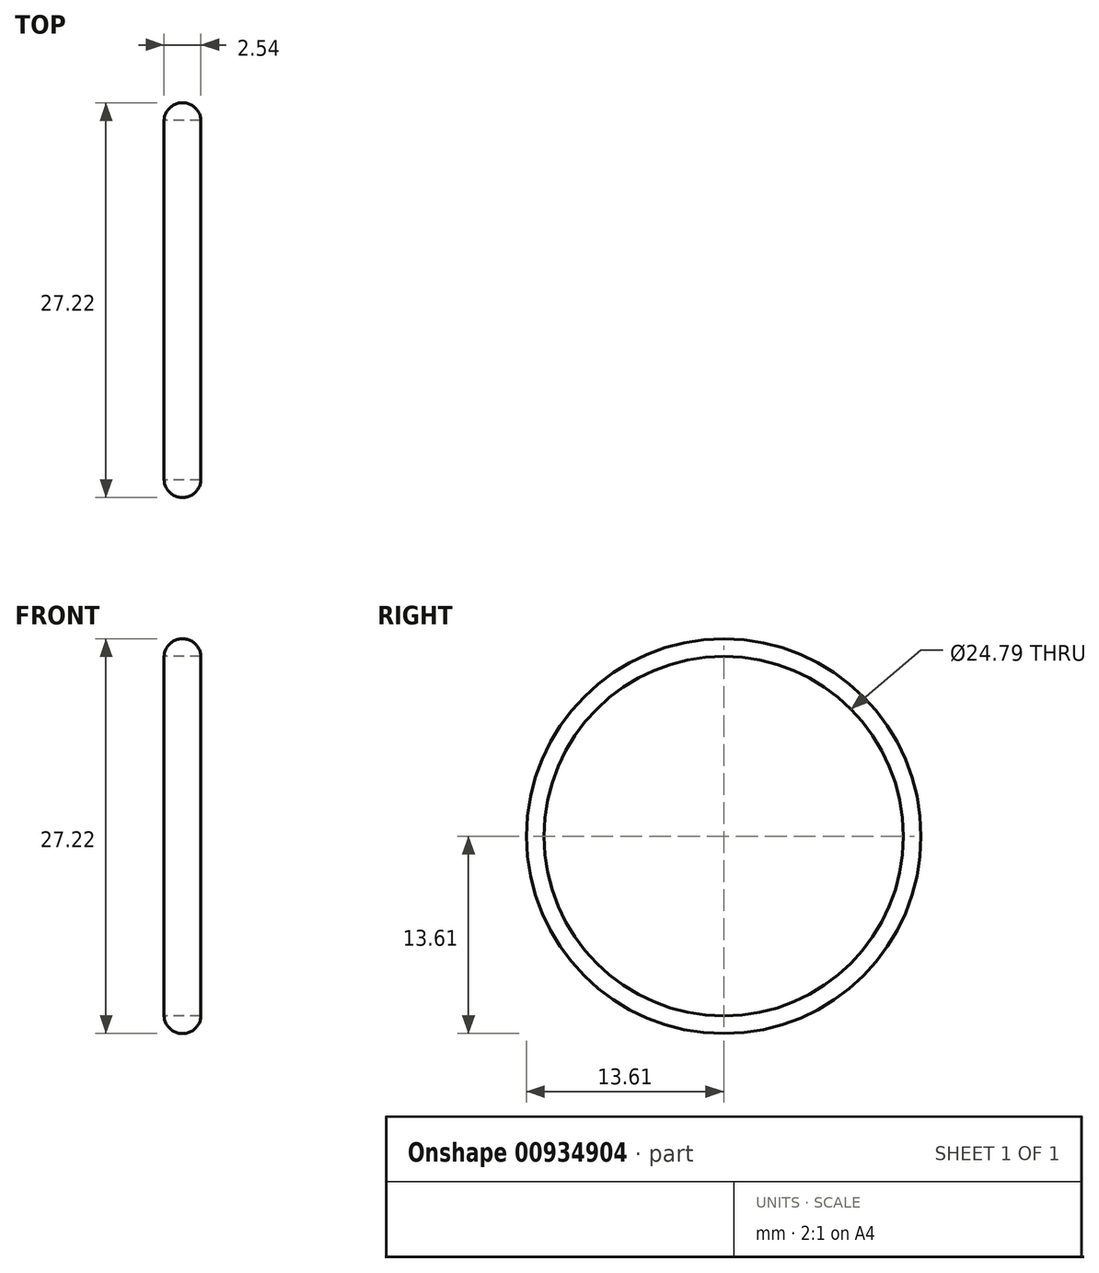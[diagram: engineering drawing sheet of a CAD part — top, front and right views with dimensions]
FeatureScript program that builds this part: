
annotation { "Feature Type Name" : "Feature", "Feature Type Description" : "" }
export const myFeature = defineFeature(function(context is Context, id is Id, definition is map)
    precondition{}
    {
        {
            var Q0;
            Q0=qCreatedBy(makeId("Right.planeOp"),FACE);
            var sketch = newSketch(context, id + "F0", { "sketchPlane" : qUnion([Q0])});
            skCircle(sketch, "E0", {"center": v(0, 0) * mm, "radius": 13.61 * mm});
            skSolve(sketch);
        }
        {
            var Q0;
            Q0=makeQuery(id+"F0.imprint","IMPRINT",FACE,{"disambiguationData":[TD([[makeQuery(id+"F0.imprint","IMPRINT",EDGE,{"derivedFrom":sQuery(id+"F0.wireOp",EDGE,"E0")}),1.0]])]});
            var sketch = newSketch(context, id + "F1", { "sketchPlane" : qUnion([Q0])});
            skCircle(sketch, "E1", {"center": v(0, 0) * mm, "radius": 12.4 * mm});
            skSolve(sketch);
        }
        {
            var Q0;
            Q0=makeQuery(id+"F0.imprint","IMPRINT",FACE,{"disambiguationData":[TD([[makeQuery(id+"F0.imprint","IMPRINT",EDGE,{"derivedFrom":sQuery(id+"F0.wireOp",EDGE,"E0")}),1.0]])]});
            extrude(context, id + "F2", {"entities" : qUnion([Q0]), "depth" : 2.54 * mm, "offsetDistance" : 25.4 * mm});
        }
        {
            var Q0;
            Q0=makeQuery(id+"F1.imprint","IMPRINT",FACE,{"disambiguationData":[TD([[makeQuery(id+"F1.imprint","IMPRINT",EDGE,{"derivedFrom":sQuery(id+"F1.wireOp",EDGE,"E1")}),1.0]])]});
            var Q1;
            Q1=sQuery(id+"F1.wireOp",EDGE,"E1");
            extrude(context, id + "F3", {"entities" : qUnion([Q0]), "operationType" : NewBodyOperationType.REMOVE, "surfaceEntities" : qUnion([Q1]), "depth" : 25.4 * mm, "offsetDistance" : 25.4 * mm});
        }
        {
            var Q0;
            Q0=makeQuery(id+"F2.opExtrude","CAP_EDGE",EDGE,{"disambiguationData":[OSD([sQuery(id+"F0.wireOp",EDGE,"E0")])],"isStart":true});
            var Q1;
            Q1=makeQuery(id+"F2.opExtrude","CAP_EDGE",EDGE,{"disambiguationData":[OSD([sQuery(id+"F0.wireOp",EDGE,"E0")])],"isStart":false});
            var Q2;
            Q2=makeQuery(id+"F2.opExtrude","SWEPT_FACE",FACE,{"disambiguationData":[OSD([sQuery(id+"F0.wireOp",EDGE,"E0")])]});
            fillet(context, id + "F4", {"entities" : qUnion([Q0, Q1, Q2]), "radius" : 1.27 * mm, "tangentPropagation" : true, "allowEdgeOverflow" : false});
        }
    });
